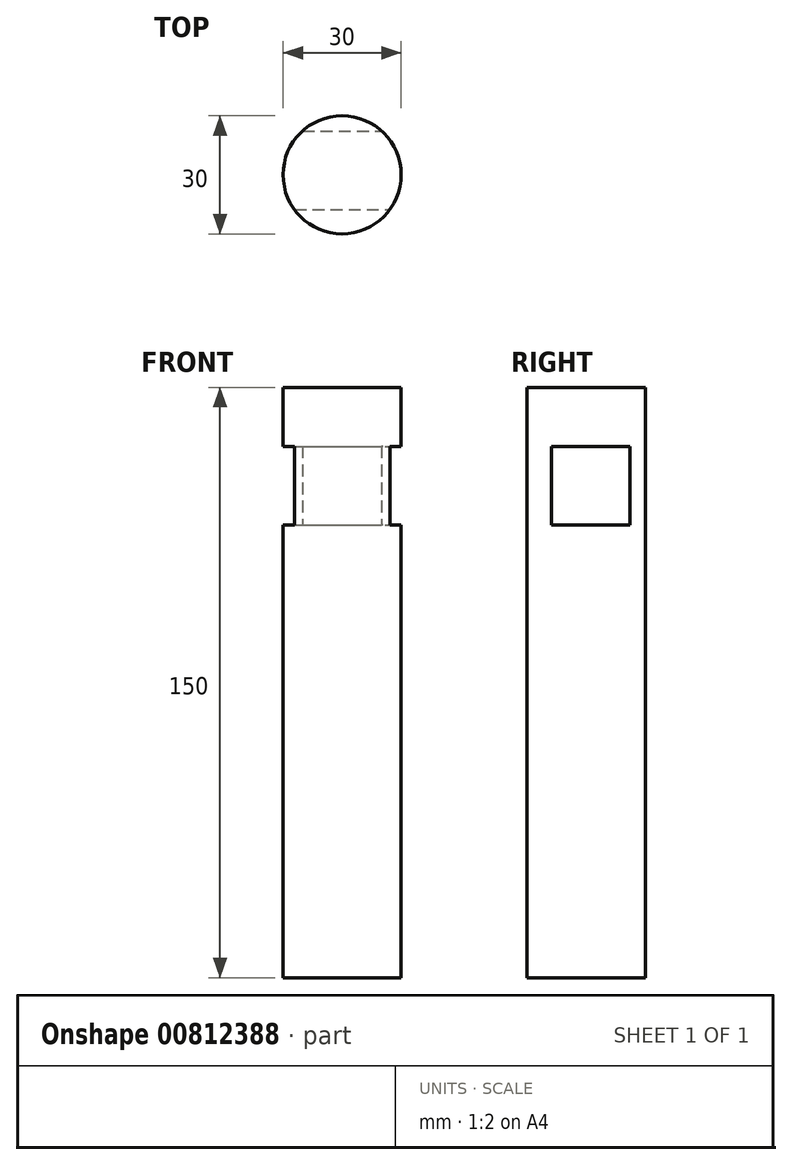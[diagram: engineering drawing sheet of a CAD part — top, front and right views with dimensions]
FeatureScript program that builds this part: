
annotation { "Feature Type Name" : "Feature", "Feature Type Description" : "" }
export const myFeature = defineFeature(function(context is Context, id is Id, definition is map)
    precondition{}
    {
        {
            var Q0;
            Q0=qCreatedBy(makeId("Top.planeOp"),FACE);
            var sketch = newSketch(context, id + "F0", { "sketchPlane" : qUnion([Q0])});
            skCircle(sketch, "E0", {"center": v(0, 0) * mm, "radius": 15 * mm});
            skSolve(sketch);
        }
        {
            var Q0;
            Q0=makeQuery(id+"F0.imprint","IMPRINT",FACE,{"disambiguationData":[TD([[makeQuery(id+"F0.imprint","IMPRINT",EDGE,{"derivedFrom":sQuery(id+"F0.wireOp",EDGE,"E0")}),1.0]])]});
            extrude(context, id + "F1", {"entities" : qUnion([Q0]), "depth" : 150 * mm, "offsetDistance" : 25 * mm});
        }
        {
            var Q0;
            Q0=qCreatedBy(makeId("Right.planeOp"),FACE);
            var sketch = newSketch(context, id + "F2", { "sketchPlane" : qUnion([Q0])});
            skLineSegment(sketch, "E1.bottom", {"start": v(-8.86, 135) * mm, "end": v(11.14, 135) * mm});
            skLineSegment(sketch, "E1.top", {"start": v(-8.86, 115) * mm, "end": v(11.14, 115) * mm});
            skLineSegment(sketch, "E1.left", {"start": v(-8.86, 135) * mm, "end": v(-8.86, 115) * mm});
            skLineSegment(sketch, "E1.right", {"start": v(11.14, 135) * mm, "end": v(11.14, 115) * mm});
            skSolve(sketch);
        }
        {
            var Q0;
            Q0 = qSketchRegion(id + "F2", true);
            extrude(context, id + "F3", {"entities" : qUnion([Q0]), "operationType" : NewBodyOperationType.REMOVE, "oppositeDirection" : true, "depth" : 25 * mm, "offsetDistance" : 25 * mm});
        }
        {
            var Q0;
            Q0 = qSketchRegion(id + "F2", true);
            extrude(context, id + "F4", {"entities" : qUnion([Q0]), "operationType" : NewBodyOperationType.REMOVE, "depth" : 25 * mm, "offsetDistance" : 25 * mm});
        }
    });
